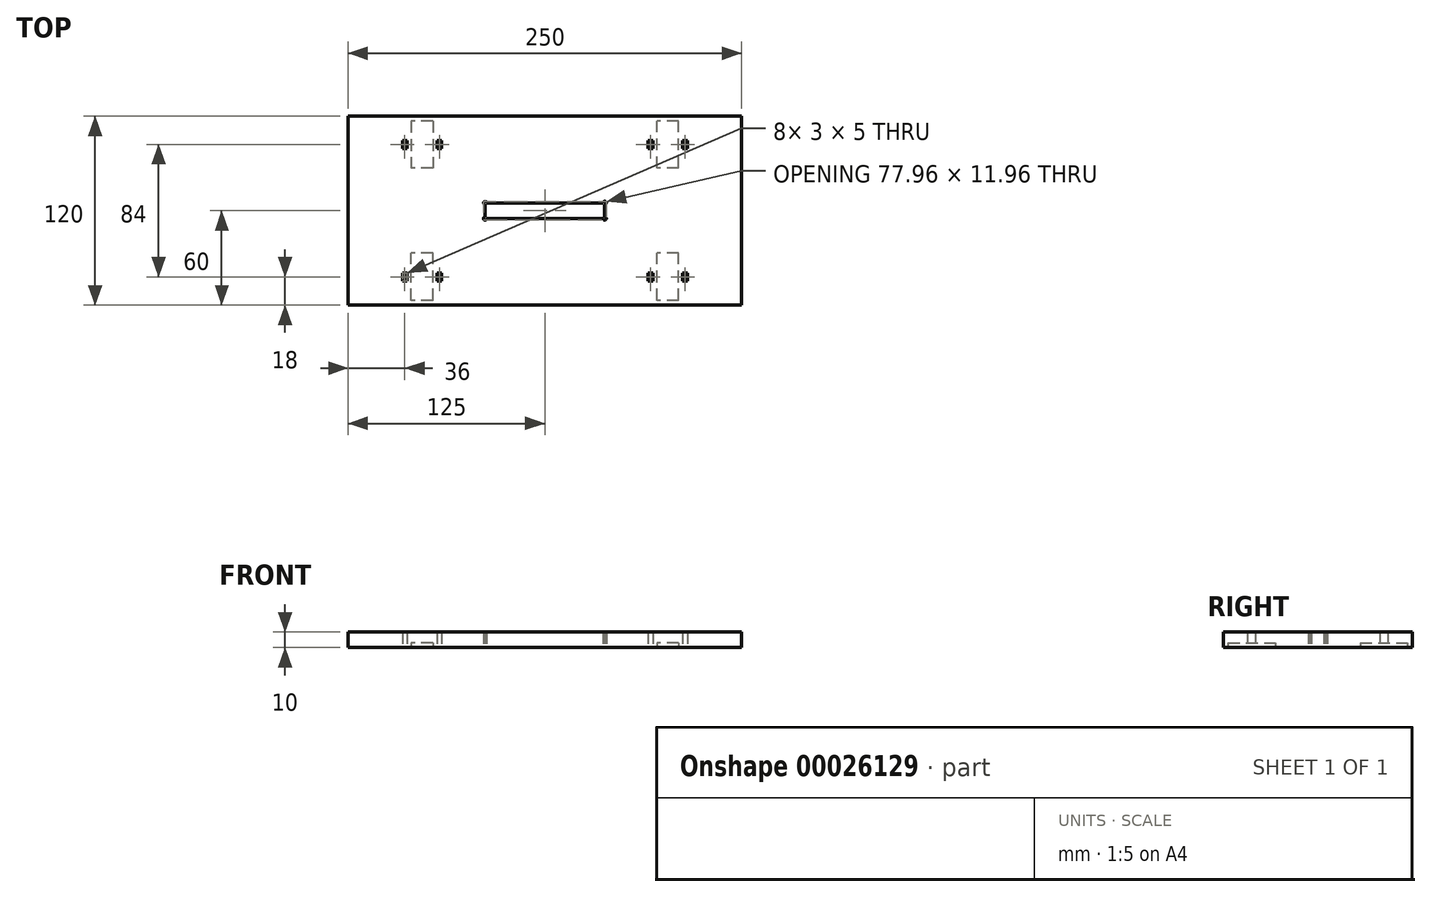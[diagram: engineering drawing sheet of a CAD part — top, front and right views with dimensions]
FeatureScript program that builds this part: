
annotation { "Feature Type Name" : "Feature", "Feature Type Description" : "" }
export const myFeature = defineFeature(function(context is Context, id is Id, definition is map)
    precondition{}
    {
        {
            var Q0;
            Q0=qCreatedBy(makeId("Top.planeOp"),FACE);
            var sketch = newSketch(context, id + "F0", { "sketchPlane" : qUnion([Q0])});
            skLineSegment(sketch, "E0.rect.bottom", {"start": v(125, -60) * mm, "end": v(-125, -60) * mm});
            skLineSegment(sketch, "E0.rect.top", {"start": v(125, 60) * mm, "end": v(-125, 60) * mm});
            skLineSegment(sketch, "E0.rect.left", {"start": v(125, -60) * mm, "end": v(125, 60) * mm});
            skLineSegment(sketch, "E0.rect.right", {"start": v(-125, -60) * mm, "end": v(-125, 60) * mm});
            skPoint(sketch, "E0.rect.middle", {"position": v(0, 0) * mm});
            skLineSegment(sketch, "E1", {"start": v(-78, 60) * mm, "end": v(-78, -60) * mm, "construction": true});
            skLineSegment(sketch, "E2", {"start": v(-78, -60) * mm, "end": v(78, 60) * mm, "construction": true});
            skLineSegment(sketch, "E3", {"start": v(78, 60) * mm, "end": v(78, -60) * mm, "construction": true});
            skLineSegment(sketch, "E4", {"start": v(-125, 57) * mm, "end": v(125, 57) * mm, "construction": true});
            skLineSegment(sketch, "E5", {"start": v(-125, -57) * mm, "end": v(125, -57) * mm, "construction": true});
            skLineSegment(sketch, "E6.rect.bottom", {"start": v(-71.07, 57) * mm, "end": v(-84.93, 57) * mm});
            skLineSegment(sketch, "E6.rect.top", {"start": v(-71.07, 27) * mm, "end": v(-84.93, 27) * mm});
            skLineSegment(sketch, "E6.rect.left", {"start": v(-71.07, 57) * mm, "end": v(-71.07, 27) * mm});
            skLineSegment(sketch, "E6.rect.right", {"start": v(-84.93, 57) * mm, "end": v(-84.93, 27) * mm});
            skPoint(sketch, "E6.rect.middle", {"position": v(-78, 42) * mm});
            skLineSegment(sketch, "E7.rect.bottom", {"start": v(-71.07, -57) * mm, "end": v(-84.93, -57) * mm});
            skLineSegment(sketch, "E7.rect.top", {"start": v(-71.07, -27) * mm, "end": v(-84.93, -27) * mm});
            skLineSegment(sketch, "E7.rect.left", {"start": v(-71.07, -57) * mm, "end": v(-71.07, -27) * mm});
            skLineSegment(sketch, "E7.rect.right", {"start": v(-84.93, -57) * mm, "end": v(-84.93, -27) * mm});
            skPoint(sketch, "E7.rect.middle", {"position": v(-78, -42) * mm});
            skLineSegment(sketch, "E8.rect.bottom", {"start": v(84.93, 27) * mm, "end": v(71.07, 27) * mm});
            skLineSegment(sketch, "E8.rect.top", {"start": v(84.93, 57) * mm, "end": v(71.07, 57) * mm});
            skLineSegment(sketch, "E8.rect.left", {"start": v(84.93, 27) * mm, "end": v(84.93, 57) * mm});
            skLineSegment(sketch, "E8.rect.right", {"start": v(71.07, 27) * mm, "end": v(71.07, 57) * mm});
            skPoint(sketch, "E8.rect.middle", {"position": v(78, 42) * mm});
            skLineSegment(sketch, "E9.rect.bottom", {"start": v(84.93, -57) * mm, "end": v(71.07, -57) * mm});
            skLineSegment(sketch, "E9.rect.top", {"start": v(84.93, -27) * mm, "end": v(71.07, -27) * mm});
            skLineSegment(sketch, "E9.rect.left", {"start": v(84.93, -57) * mm, "end": v(84.93, -27) * mm});
            skLineSegment(sketch, "E9.rect.right", {"start": v(71.07, -57) * mm, "end": v(71.07, -27) * mm});
            skPoint(sketch, "E9.rect.middle", {"position": v(78, -42) * mm});
            skCircle(sketch, "E10", {"center": v(-201.5, 0) * mm, "radius": 9.5 * mm, "construction": true});
            skLineSegment(sketch, "E11", {"start": v(-227.26, 9.5) * mm, "end": v(-166.14, 9.5) * mm, "construction": true});
            skLineSegment(sketch, "E12", {"start": v(-166.14, 6.5) * mm, "end": v(-227.26, 6.5) * mm, "construction": true});
            skLineSegment(sketch, "E13", {"start": v(-208.44, 9.5) * mm, "end": v(-208.44, 6.5) * mm});
            skLineSegment(sketch, "E14", {"start": v(-194.58, 9.5) * mm, "end": v(-194.58, 6.5) * mm});
            skLineSegment(sketch, "E15.rect.bottom", {"start": v(37, 5) * mm, "end": v(-37, 5) * mm});
            skLineSegment(sketch, "E15.rect.top", {"start": v(37, -5) * mm, "end": v(-37, -5) * mm});
            skLineSegment(sketch, "E15.rect.left", {"start": v(38, 4) * mm, "end": v(38, -4) * mm});
            skLineSegment(sketch, "E15.rect.right", {"start": v(-38, 4) * mm, "end": v(-38, -4) * mm});
            skLineSegment(sketch, "E16.rect.bottom", {"start": v(87.5, -57) * mm, "end": v(68.5, -57) * mm, "construction": true});
            skLineSegment(sketch, "E16.rect.top", {"start": v(87.5, -27) * mm, "end": v(68.5, -27) * mm, "construction": true});
            skLineSegment(sketch, "E16.rect.left", {"start": v(87.5, -57) * mm, "end": v(87.5, -44.5) * mm, "construction": true});
            skLineSegment(sketch, "E16.rect.right", {"start": v(68.5, -57) * mm, "end": v(68.5, -44.5) * mm, "construction": true});
            skLineSegment(sketch, "E17.rect.bottom", {"start": v(88.5, -39.5) * mm, "end": v(89.5, -39.5) * mm, "construction": true});
            skLineSegment(sketch, "E17.rect.top", {"start": v(88.5, -44.5) * mm, "end": v(89.5, -44.5) * mm, "construction": true});
            skLineSegment(sketch, "E17.rect.left", {"start": v(87.5, -40.5) * mm, "end": v(87.5, -44.5) * mm, "construction": true});
            skLineSegment(sketch, "E17.rect.right", {"start": v(90.5, -40.5) * mm, "end": v(90.5, -43.5) * mm, "construction": true});
            skPoint(sketch, "E17.rect.middle", {"position": v(89, -42) * mm});
            skLineSegment(sketch, "E18.rect.bottom", {"start": v(67.5, -39.5) * mm, "end": v(66.5, -39.5) * mm, "construction": true});
            skLineSegment(sketch, "E18.rect.top", {"start": v(67.5, -44.5) * mm, "end": v(66.5, -44.5) * mm, "construction": true});
            skLineSegment(sketch, "E18.rect.left", {"start": v(68.5, -40.5) * mm, "end": v(68.5, -44.5) * mm, "construction": true});
            skLineSegment(sketch, "E18.rect.right", {"start": v(65.5, -40.5) * mm, "end": v(65.5, -43.5) * mm, "construction": true});
            skPoint(sketch, "E18.rect.middle", {"position": v(67, -42) * mm});
            skLineSegment(sketch, "E19", {"start": v(0, -60) * mm, "end": v(0, 0) * mm, "construction": true});
            skLineSegment(sketch, "E20", {"start": v(0, 0) * mm, "end": v(125, 0) * mm, "construction": true});
            skLineSegment(sketch, "E21.MirrorCS", {"start": v(87.5, 40.5) * mm, "end": v(87.5, 43.5) * mm, "construction": true});
            skLineSegment(sketch, "E22.MirrorCS", {"start": v(88.5, 44.5) * mm, "end": v(89.5, 44.5) * mm, "construction": true});
            skLineSegment(sketch, "E23.MirrorCS", {"start": v(90.5, 40.5) * mm, "end": v(90.5, 43.5) * mm, "construction": true});
            skLineSegment(sketch, "E24.MirrorCS", {"start": v(88.5, 39.5) * mm, "end": v(89.5, 39.5) * mm, "construction": true});
            skLineSegment(sketch, "E25.MirrorCS", {"start": v(68.5, 40.5) * mm, "end": v(68.5, 43.5) * mm, "construction": true});
            skLineSegment(sketch, "E26.MirrorCS", {"start": v(67.5, 44.5) * mm, "end": v(66.5, 44.5) * mm, "construction": true});
            skLineSegment(sketch, "E27.MirrorCS", {"start": v(65.5, 40.5) * mm, "end": v(65.5, 43.5) * mm, "construction": true});
            skLineSegment(sketch, "E28.MirrorCS", {"start": v(67.5, 39.5) * mm, "end": v(66.5, 39.5) * mm, "construction": true});
            skLineSegment(sketch, "E29.MirrorCS", {"start": v(-87.5, -40.5) * mm, "end": v(-87.5, -43.5) * mm, "construction": true});
            skLineSegment(sketch, "E30.MirrorCS", {"start": v(-88.5, -44.5) * mm, "end": v(-89.5, -44.5) * mm, "construction": true});
            skLineSegment(sketch, "E31.MirrorCS", {"start": v(-90.5, -40.5) * mm, "end": v(-90.5, -43.5) * mm, "construction": true});
            skLineSegment(sketch, "E32.MirrorCS", {"start": v(-88.5, -39.5) * mm, "end": v(-89.5, -39.5) * mm, "construction": true});
            skLineSegment(sketch, "E33.MirrorCS", {"start": v(-67.5, -39.5) * mm, "end": v(-66.5, -39.5) * mm, "construction": true});
            skLineSegment(sketch, "E34.MirrorCS", {"start": v(-68.5, -40.5) * mm, "end": v(-68.5, -43.5) * mm, "construction": true});
            skLineSegment(sketch, "E35.MirrorCS", {"start": v(-67.5, -44.5) * mm, "end": v(-66.5, -44.5) * mm, "construction": true});
            skLineSegment(sketch, "E36.MirrorCS", {"start": v(-65.5, -40.5) * mm, "end": v(-65.5, -43.5) * mm, "construction": true});
            skLineSegment(sketch, "E37.MirrorCS", {"start": v(-87.5, 40.5) * mm, "end": v(-87.5, 43.5) * mm, "construction": true});
            skLineSegment(sketch, "E38.MirrorCS", {"start": v(-88.5, 39.5) * mm, "end": v(-89.5, 39.5) * mm, "construction": true});
            skLineSegment(sketch, "E39.MirrorCS", {"start": v(-90.5, 40.5) * mm, "end": v(-90.5, 43.5) * mm, "construction": true});
            skLineSegment(sketch, "E40.MirrorCS", {"start": v(-88.5, 44.5) * mm, "end": v(-89.5, 44.5) * mm, "construction": true});
            skLineSegment(sketch, "E41.MirrorCS", {"start": v(-67.5, 44.5) * mm, "end": v(-66.5, 44.5) * mm, "construction": true});
            skLineSegment(sketch, "E42.MirrorCS", {"start": v(-68.5, 40.5) * mm, "end": v(-68.5, 43.5) * mm, "construction": true});
            skLineSegment(sketch, "E43.MirrorCS", {"start": v(-67.5, 39.5) * mm, "end": v(-66.5, 39.5) * mm, "construction": true});
            skLineSegment(sketch, "E44.MirrorCS", {"start": v(-65.5, 40.5) * mm, "end": v(-65.5, 43.5) * mm, "construction": true});
            skArc(sketch, "E45", {"start": v(-37, 5) * mm, "mid": v(-38.7, 5.7) * mm, "end": v(-38, 4) * mm});
            skArc(sketch, "E46", {"start": v(-38, -4) * mm, "mid": v(-38.7, -5.7) * mm, "end": v(-37, -5) * mm});
            skArc(sketch, "E47", {"start": v(38, 4) * mm, "mid": v(38.7, 5.7) * mm, "end": v(37, 5) * mm});
            skArc(sketch, "E48", {"start": v(37, -5) * mm, "mid": v(38.7, -5.7) * mm, "end": v(38, -4) * mm});
            skArc(sketch, "E49", {"start": v(66.5, 44.5) * mm, "mid": v(64.8, 45.2) * mm, "end": v(65.5, 43.5) * mm, "construction": true});
            skArc(sketch, "E50", {"start": v(65.5, 40.5) * mm, "mid": v(64.8, 38.8) * mm, "end": v(66.5, 39.5) * mm, "construction": true});
            skArc(sketch, "E51", {"start": v(67.5, 39.5) * mm, "mid": v(69.2, 38.8) * mm, "end": v(68.5, 40.5) * mm, "construction": true});
            skArc(sketch, "E52", {"start": v(68.5, 43.5) * mm, "mid": v(69.2, 45.2) * mm, "end": v(67.5, 44.5) * mm, "construction": true});
            skArc(sketch, "E53", {"start": v(88.5, 44.5) * mm, "mid": v(86.8, 45.2) * mm, "end": v(87.5, 43.5) * mm, "construction": true});
            skArc(sketch, "E54", {"start": v(90.5, 43.5) * mm, "mid": v(91.2, 45.2) * mm, "end": v(89.5, 44.5) * mm, "construction": true});
            skArc(sketch, "E55", {"start": v(89.5, 39.5) * mm, "mid": v(91.2, 38.8) * mm, "end": v(90.5, 40.5) * mm, "construction": true});
            skArc(sketch, "E56", {"start": v(87.5, 40.5) * mm, "mid": v(86.8, 38.8) * mm, "end": v(88.5, 39.5) * mm, "construction": true});
            skArc(sketch, "E57", {"start": v(66.5, -39.5) * mm, "mid": v(64.8, -38.8) * mm, "end": v(65.5, -40.5) * mm, "construction": true});
            skArc(sketch, "E58", {"start": v(68.5, -40.5) * mm, "mid": v(69.2, -38.8) * mm, "end": v(67.5, -39.5) * mm, "construction": true});
            skArc(sketch, "E59", {"start": v(65.5, -43.5) * mm, "mid": v(64.8, -45.2) * mm, "end": v(66.5, -44.5) * mm, "construction": true});
            skArc(sketch, "E60", {"start": v(67.5, -44.5) * mm, "mid": v(69.2, -45.2) * mm, "end": v(68.5, -43.5) * mm, "construction": true});
            skArc(sketch, "E61", {"start": v(88.5, -39.5) * mm, "mid": v(86.8, -38.8) * mm, "end": v(87.5, -40.5) * mm, "construction": true});
            skArc(sketch, "E62", {"start": v(90.5, -40.5) * mm, "mid": v(91.2, -38.8) * mm, "end": v(89.5, -39.5) * mm, "construction": true});
            skArc(sketch, "E63", {"start": v(89.5, -44.5) * mm, "mid": v(91.2, -45.2) * mm, "end": v(90.5, -43.5) * mm, "construction": true});
            skArc(sketch, "E64", {"start": v(87.5, -43.5) * mm, "mid": v(86.8, -45.2) * mm, "end": v(88.5, -44.5) * mm, "construction": true});
            skArc(sketch, "E65", {"start": v(-89.5, 44.5) * mm, "mid": v(-91.2, 45.2) * mm, "end": v(-90.5, 43.5) * mm, "construction": true});
            skArc(sketch, "E66", {"start": v(-87.5, 43.5) * mm, "mid": v(-86.8, 45.2) * mm, "end": v(-88.5, 44.5) * mm, "construction": true});
            skArc(sketch, "E67", {"start": v(-90.5, 40.5) * mm, "mid": v(-91.2, 38.8) * mm, "end": v(-89.5, 39.5) * mm, "construction": true});
            skArc(sketch, "E68", {"start": v(-88.5, 39.5) * mm, "mid": v(-86.8, 38.8) * mm, "end": v(-87.5, 40.5) * mm, "construction": true});
            skArc(sketch, "E69", {"start": v(-67.5, 44.5) * mm, "mid": v(-69.2, 45.2) * mm, "end": v(-68.5, 43.5) * mm, "construction": true});
            skArc(sketch, "E70", {"start": v(-65.5, 43.5) * mm, "mid": v(-64.8, 45.2) * mm, "end": v(-66.5, 44.5) * mm, "construction": true});
            skArc(sketch, "E71", {"start": v(-68.5, 40.5) * mm, "mid": v(-69.2, 38.8) * mm, "end": v(-67.5, 39.5) * mm, "construction": true});
            skArc(sketch, "E72", {"start": v(-66.5, 39.5) * mm, "mid": v(-64.8, 38.8) * mm, "end": v(-65.5, 40.5) * mm, "construction": true});
            skArc(sketch, "E73", {"start": v(-89.5, -39.5) * mm, "mid": v(-91.2, -38.8) * mm, "end": v(-90.5, -40.5) * mm, "construction": true});
            skArc(sketch, "E74", {"start": v(-87.5, -40.5) * mm, "mid": v(-86.8, -38.8) * mm, "end": v(-88.5, -39.5) * mm, "construction": true});
            skArc(sketch, "E75", {"start": v(-90.5, -43.5) * mm, "mid": v(-91.2, -45.2) * mm, "end": v(-89.5, -44.5) * mm, "construction": true});
            skArc(sketch, "E76", {"start": v(-88.5, -44.5) * mm, "mid": v(-86.8, -45.2) * mm, "end": v(-87.5, -43.5) * mm, "construction": true});
            skArc(sketch, "E77", {"start": v(-67.5, -39.5) * mm, "mid": v(-69.2, -38.8) * mm, "end": v(-68.5, -40.5) * mm, "construction": true});
            skArc(sketch, "E78", {"start": v(-65.5, -40.5) * mm, "mid": v(-64.8, -38.8) * mm, "end": v(-66.5, -39.5) * mm, "construction": true});
            skArc(sketch, "E79", {"start": v(-68.5, -43.5) * mm, "mid": v(-69.2, -45.2) * mm, "end": v(-67.5, -44.5) * mm, "construction": true});
            skArc(sketch, "E80", {"start": v(-66.5, -44.5) * mm, "mid": v(-64.8, -45.2) * mm, "end": v(-65.5, -43.5) * mm, "construction": true});
            skLineSegment(sketch, "E81.trimOffspring", {"start": v(68.5, -43.5) * mm, "end": v(68.5, -27) * mm, "construction": true});
            skLineSegment(sketch, "E82.trimOffspring", {"start": v(87.5, -43.5) * mm, "end": v(87.5, -27) * mm, "construction": true});
            skLineSegment(sketch, "E83.bottom", {"start": v(-90.5, -44.5) * mm, "end": v(-87.5, -44.5) * mm});
            skLineSegment(sketch, "E83.top", {"start": v(-90.5, -39.5) * mm, "end": v(-87.5, -39.5) * mm});
            skLineSegment(sketch, "E83.left", {"start": v(-90.5, -44.5) * mm, "end": v(-90.5, -39.5) * mm});
            skLineSegment(sketch, "E83.right", {"start": v(-87.5, -44.5) * mm, "end": v(-87.5, -39.5) * mm});
            skLineSegment(sketch, "E84.bottom", {"start": v(-68.5, 44.5) * mm, "end": v(-65.5, 44.5) * mm});
            skLineSegment(sketch, "E84.top", {"start": v(-68.5, 39.5) * mm, "end": v(-65.5, 39.5) * mm});
            skLineSegment(sketch, "E84.left", {"start": v(-68.5, 44.5) * mm, "end": v(-68.5, 39.5) * mm});
            skLineSegment(sketch, "E84.right", {"start": v(-65.5, 44.5) * mm, "end": v(-65.5, 39.5) * mm});
            skLineSegment(sketch, "E85.bottom", {"start": v(-90.5, 44.5) * mm, "end": v(-87.5, 44.5) * mm});
            skLineSegment(sketch, "E85.top", {"start": v(-90.5, 39.5) * mm, "end": v(-87.5, 39.5) * mm});
            skLineSegment(sketch, "E85.left", {"start": v(-90.5, 44.5) * mm, "end": v(-90.5, 39.5) * mm});
            skLineSegment(sketch, "E85.right", {"start": v(-87.5, 44.5) * mm, "end": v(-87.5, 39.5) * mm});
            skLineSegment(sketch, "E86.bottom", {"start": v(-68.5, -39.5) * mm, "end": v(-65.5, -39.5) * mm});
            skLineSegment(sketch, "E86.top", {"start": v(-68.5, -44.5) * mm, "end": v(-65.5, -44.5) * mm});
            skLineSegment(sketch, "E86.left", {"start": v(-68.5, -39.5) * mm, "end": v(-68.5, -44.5) * mm});
            skLineSegment(sketch, "E86.right", {"start": v(-65.5, -39.5) * mm, "end": v(-65.5, -44.5) * mm});
            skLineSegment(sketch, "E87.bottom", {"start": v(65.5, -39.5) * mm, "end": v(68.5, -39.5) * mm});
            skLineSegment(sketch, "E87.top", {"start": v(65.5, -44.5) * mm, "end": v(68.5, -44.5) * mm});
            skLineSegment(sketch, "E87.left", {"start": v(65.5, -39.5) * mm, "end": v(65.5, -44.5) * mm});
            skLineSegment(sketch, "E87.right", {"start": v(68.5, -39.5) * mm, "end": v(68.5, -44.5) * mm});
            skLineSegment(sketch, "E88.bottom", {"start": v(87.5, -39.5) * mm, "end": v(90.5, -39.5) * mm});
            skLineSegment(sketch, "E88.top", {"start": v(87.5, -44.5) * mm, "end": v(90.5, -44.5) * mm});
            skLineSegment(sketch, "E88.left", {"start": v(87.5, -39.5) * mm, "end": v(87.5, -44.5) * mm});
            skLineSegment(sketch, "E88.right", {"start": v(90.5, -39.5) * mm, "end": v(90.5, -44.5) * mm});
            skLineSegment(sketch, "E89.bottom", {"start": v(87.5, 44.5) * mm, "end": v(90.5, 44.5) * mm});
            skLineSegment(sketch, "E89.top", {"start": v(87.5, 39.5) * mm, "end": v(90.5, 39.5) * mm});
            skLineSegment(sketch, "E89.left", {"start": v(87.5, 44.5) * mm, "end": v(87.5, 39.5) * mm});
            skLineSegment(sketch, "E89.right", {"start": v(90.5, 44.5) * mm, "end": v(90.5, 39.5) * mm});
            skLineSegment(sketch, "E90.bottom", {"start": v(65.5, 44.5) * mm, "end": v(68.5, 44.5) * mm});
            skLineSegment(sketch, "E90.top", {"start": v(65.5, 39.5) * mm, "end": v(68.5, 39.5) * mm});
            skLineSegment(sketch, "E90.left", {"start": v(65.5, 44.5) * mm, "end": v(65.5, 39.5) * mm});
            skLineSegment(sketch, "E90.right", {"start": v(68.5, 44.5) * mm, "end": v(68.5, 39.5) * mm});
            skSolve(sketch);
        }
        {
            var Q0;
            Q0=makeQuery(id+"F0.imprint","IMPRINT",FACE,{"disambiguationData":[TD([[makeQuery(id+"F0.imprint","IMPRINT",EDGE,{"derivedFrom":sQuery(id+"F0.wireOp",EDGE,"E0.rect.bottom")}),-1.0]])]});
            var Q1;
            Q1=makeQuery(id+"F0.imprint","IMPRINT",FACE,{"disambiguationData":[TD([[makeQuery(id+"F0.imprint","IMPRINT",EDGE,{"derivedFrom":sQuery(id+"F0.wireOp",EDGE,"E6.rect.bottom")}),1.0]])]});
            var Q2;
            Q2=makeQuery(id+"F0.imprint","IMPRINT",FACE,{"disambiguationData":[TD([[makeQuery(id+"F0.imprint","IMPRINT",EDGE,{"derivedFrom":sQuery(id+"F0.wireOp",EDGE,"E7.rect.bottom")}),-1.0]])]});
            var Q3;
            Q3=makeQuery(id+"F0.imprint","IMPRINT",FACE,{"disambiguationData":[TD([[makeQuery(id+"F0.imprint","IMPRINT",EDGE,{"derivedFrom":sQuery(id+"F0.wireOp",EDGE,"E8.rect.bottom")}),-1.0]])]});
            var Q4;
            Q4=makeQuery(id+"F0.imprint","IMPRINT",FACE,{"disambiguationData":[TD([[makeQuery(id+"F0.imprint","IMPRINT",EDGE,{"derivedFrom":sQuery(id+"F0.wireOp",EDGE,"E9.rect.bottom")}),-1.0]])]});
            var Q5;
            Q5=makeQuery(id+"F0.imprint","IMPRINT",FACE,{"disambiguationData":[TD([[makeQuery(id+"F0.imprint","IMPRINT",EDGE,{"derivedFrom":sQuery(id+"F0.wireOp",EDGE,"E37.MirrorCS")}),1.0]])]});
            var Q6;
            Q6=makeQuery(id+"F0.imprint","IMPRINT",FACE,{"disambiguationData":[TD([[makeQuery(id+"F0.imprint","IMPRINT",EDGE,{"derivedFrom":sQuery(id+"F0.wireOp",EDGE,"E41.MirrorCS")}),-1.0]])]});
            var Q7;
            Q7=makeQuery(id+"F0.imprint","IMPRINT",FACE,{"disambiguationData":[TD([[makeQuery(id+"F0.imprint","IMPRINT",EDGE,{"derivedFrom":sQuery(id+"F0.wireOp",EDGE,"E29.MirrorCS")}),-1.0]])]});
            var Q8;
            Q8=makeQuery(id+"F0.imprint","IMPRINT",FACE,{"disambiguationData":[TD([[makeQuery(id+"F0.imprint","IMPRINT",EDGE,{"derivedFrom":sQuery(id+"F0.wireOp",EDGE,"E33.MirrorCS")}),-1.0]])]});
            var Q9;
            Q9=makeQuery(id+"F0.imprint","IMPRINT",FACE,{"disambiguationData":[TD([[makeQuery(id+"F0.imprint","IMPRINT",EDGE,{"derivedFrom":sQuery(id+"F0.wireOp",EDGE,"E25.MirrorCS")}),1.0]])]});
            var Q10;
            Q10=makeQuery(id+"F0.imprint","IMPRINT",FACE,{"disambiguationData":[TD([[makeQuery(id+"F0.imprint","IMPRINT",EDGE,{"derivedFrom":sQuery(id+"F0.wireOp",EDGE,"E21.MirrorCS")}),-1.0]])]});
            var Q11;
            Q11=makeQuery(id+"F0.imprint","IMPRINT",FACE,{"disambiguationData":[TD([[makeQuery(id+"F0.imprint","IMPRINT",EDGE,{"derivedFrom":sQuery(id+"F0.wireOp",EDGE,"E17.rect.bottom")}),-1.0]])]});
            var Q12;
            Q12=makeQuery(id+"F0.imprint","IMPRINT",FACE,{"disambiguationData":[TD([[makeQuery(id+"F0.imprint","IMPRINT",EDGE,{"derivedFrom":sQuery(id+"F0.wireOp",EDGE,"E18.rect.bottom")}),1.0]])]});
            extrude(context, id + "F1", {"entities" : qUnion([Q0, Q1, Q2, Q3, Q4, Q5, Q6, Q7, Q8, Q9, Q10, Q11, Q12]), "depth" : 10 * mm});
        }
        {
            var Q0;
            Q0=makeQuery(id+"F0.imprint","IMPRINT",FACE,{"disambiguationData":[TD([[makeQuery(id+"F0.imprint","IMPRINT",EDGE,{"derivedFrom":sQuery(id+"F0.wireOp",EDGE,"E8.rect.bottom")}),-1.0]])]});
            var Q1;
            Q1=makeQuery(id+"F0.imprint","IMPRINT",FACE,{"disambiguationData":[TD([[makeQuery(id+"F0.imprint","IMPRINT",EDGE,{"derivedFrom":sQuery(id+"F0.wireOp",EDGE,"E9.rect.bottom")}),-1.0]])]});
            var Q2;
            Q2=makeQuery(id+"F0.imprint","IMPRINT",FACE,{"disambiguationData":[TD([[makeQuery(id+"F0.imprint","IMPRINT",EDGE,{"derivedFrom":sQuery(id+"F0.wireOp",EDGE,"E6.rect.bottom")}),1.0]])]});
            var Q3;
            Q3=makeQuery(id+"F0.imprint","IMPRINT",FACE,{"disambiguationData":[TD([[makeQuery(id+"F0.imprint","IMPRINT",EDGE,{"derivedFrom":sQuery(id+"F0.wireOp",EDGE,"E7.rect.bottom")}),-1.0]])]});
            extrude(context, id + "F2", {"entities" : qUnion([Q0, Q1, Q2, Q3]), "operationType" : NewBodyOperationType.REMOVE, "depth" : 3 * mm});
        }
    });
